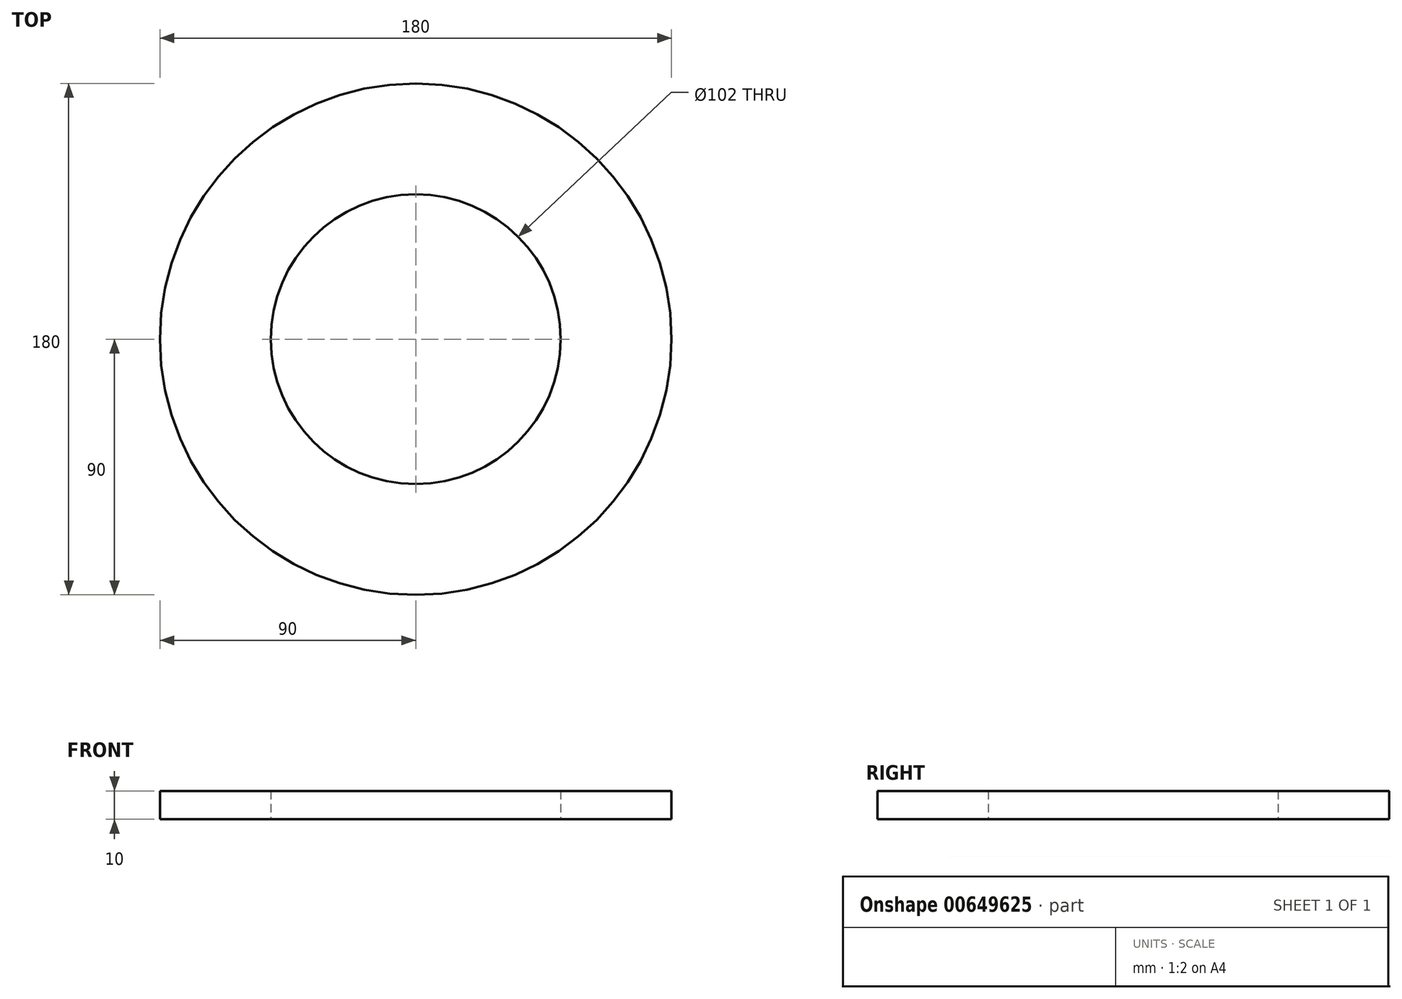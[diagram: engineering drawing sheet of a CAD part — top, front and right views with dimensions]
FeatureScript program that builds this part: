
annotation { "Feature Type Name" : "Feature", "Feature Type Description" : "" }
export const myFeature = defineFeature(function(context is Context, id is Id, definition is map)
    precondition{}
    {
        {
            var Q0;
            Q0=qCreatedBy(makeId("Top.planeOp"),FACE);
            var sketch = newSketch(context, id + "F0", { "sketchPlane" : qUnion([Q0])});
            skCircle(sketch, "E0", {"center": v(0, 0) * mm, "radius": 51 * mm});
            skCircle(sketch, "E1", {"center": v(0, 0) * mm, "radius": 90 * mm});
            skSolve(sketch);
        }
        {
            var Q0;
            Q0=makeQuery(id+"F0.imprint","IMPRINT",FACE,{"disambiguationData":[TD([[makeQuery(id+"F0.imprint","IMPRINT",EDGE,{"derivedFrom":sQuery(id+"F0.wireOp",EDGE,"E0")}),-1.0]])]});
            extrude(context, id + "F1", {"entities" : qUnion([Q0]), "depth" : 10 * mm, "offsetDistance" : 25 * mm});
        }
    });
